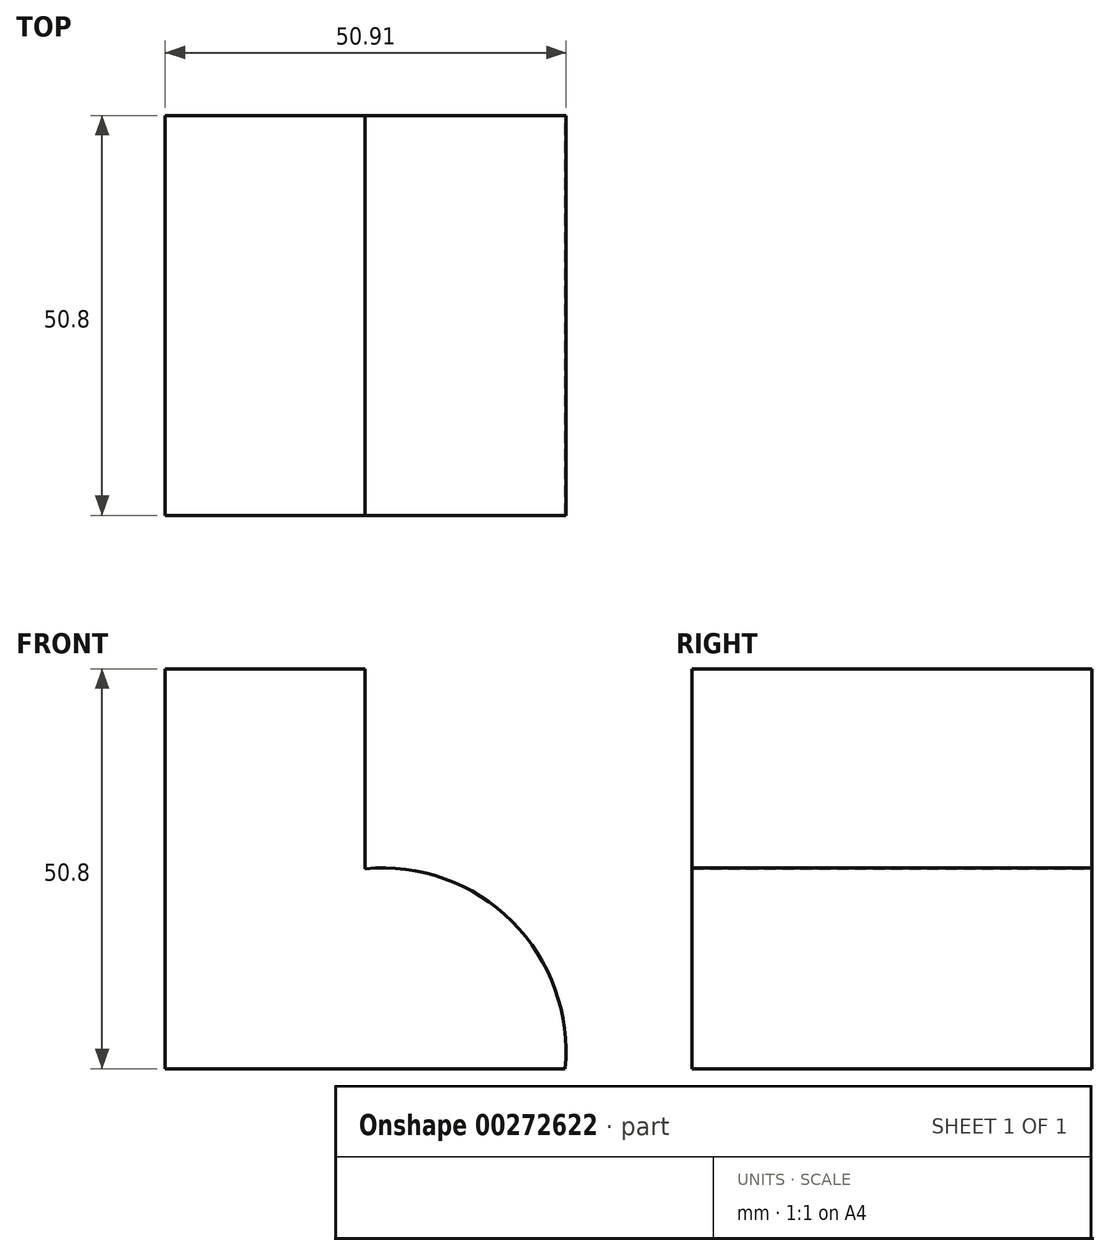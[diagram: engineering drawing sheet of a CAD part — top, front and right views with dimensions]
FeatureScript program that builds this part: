
annotation { "Feature Type Name" : "Feature", "Feature Type Description" : "" }
export const myFeature = defineFeature(function(context is Context, id is Id, definition is map)
    precondition{}
    {
        {
            var Q0;
            Q0=qCreatedBy(makeId("Front.planeOp"),FACE);
            var sketch = newSketch(context, id + "F0", { "sketchPlane" : qUnion([Q0])});
            skLineSegment(sketch, "E0", {"start": v(0, 0) * mm, "end": v(-50.8, 0) * mm});
            skLineSegment(sketch, "E1", {"start": v(-50.8, 0) * mm, "end": v(-50.8, 50.8) * mm});
            skLineSegment(sketch, "E2", {"start": v(-50.8, 50.8) * mm, "end": v(-25.4, 50.8) * mm});
            skLineSegment(sketch, "E3", {"start": v(-25.4, 50.8) * mm, "end": v(-25.4, 25.4) * mm});
            skArc(sketch, "E4", {"start": v(0, 0) * mm, "mid": v(-6.72, 18.68) * mm, "end": v(-25.4, 25.4) * mm});
            skSolve(sketch);
        }
        {
            var Q0;
            Q0 = qSketchRegion(id + "F0", true);
            extrude(context, id + "F1", {"entities" : qUnion([Q0]), "depth" : 50.8 * mm});
        }
    });
